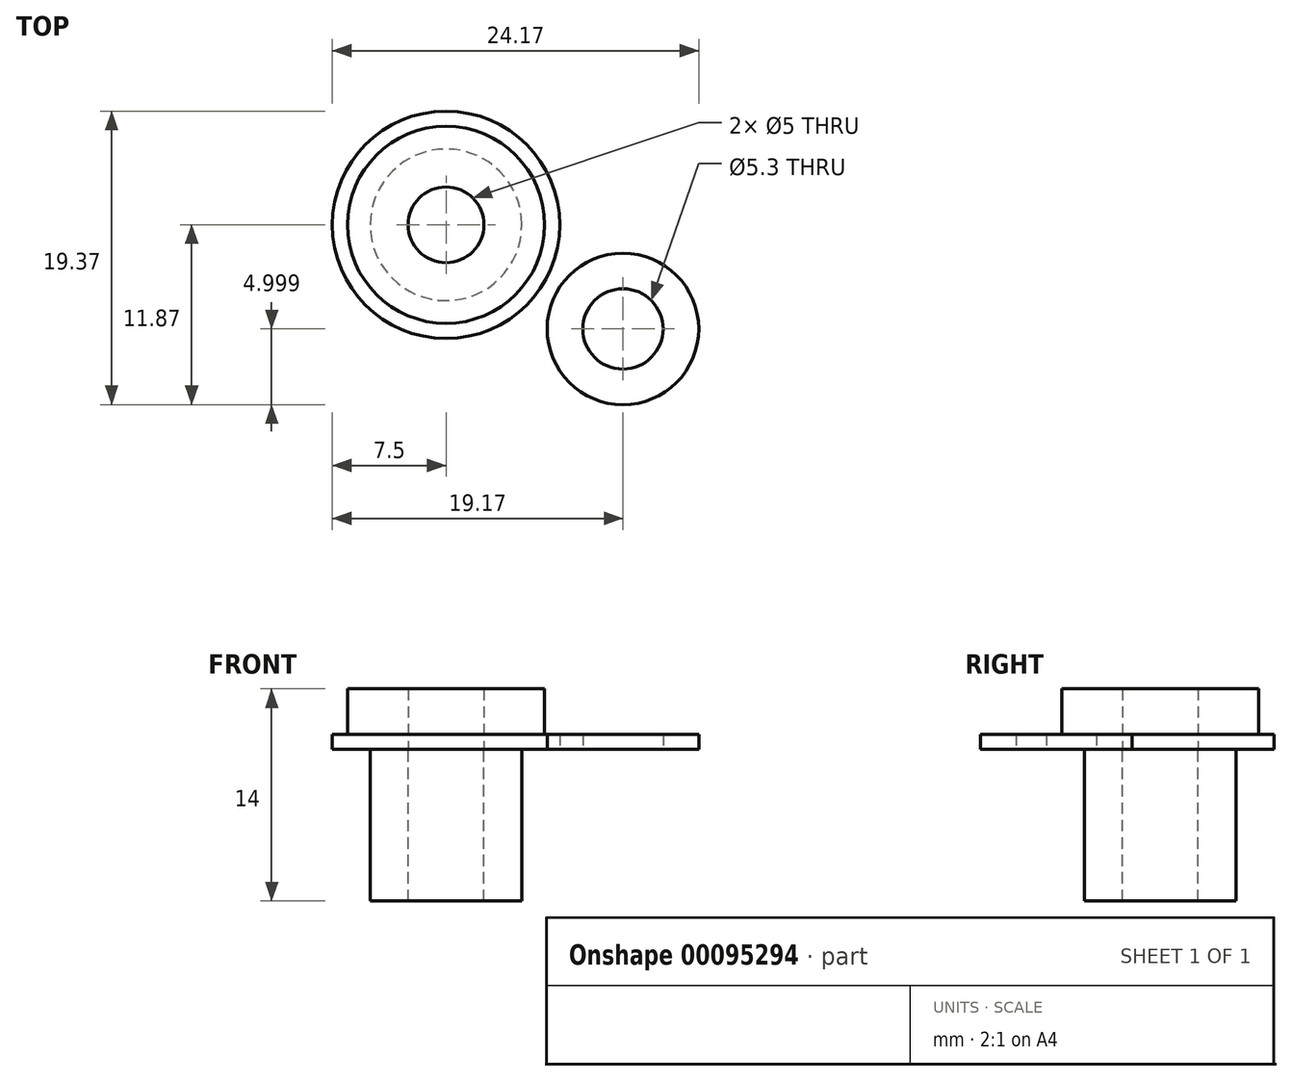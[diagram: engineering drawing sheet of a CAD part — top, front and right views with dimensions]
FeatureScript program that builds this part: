
annotation { "Feature Type Name" : "Feature", "Feature Type Description" : "" }
export const myFeature = defineFeature(function(context is Context, id is Id, definition is map)
    precondition{}
    {
        {
            var Q0;
            Q0=qCreatedBy(makeId("Top.planeOp"),FACE);
            var sketch = newSketch(context, id + "F0", { "sketchPlane" : qUnion([Q0])});
            skCircle(sketch, "E0", {"center": v(0, 0) * mm, "radius": 7.5 * mm});
            skCircle(sketch, "E1", {"center": v(0, 0) * mm, "radius": 6.5 * mm});
            skCircle(sketch, "E2", {"center": v(0, 0) * mm, "radius": 2.5 * mm});
            skSolve(sketch);
        }
        {
            var Q0;
            Q0=makeQuery(id+"F0.imprint","IMPRINT",FACE,{"disambiguationData":[TD([[makeQuery(id+"F0.imprint","IMPRINT",EDGE,{"derivedFrom":sQuery(id+"F0.wireOp",EDGE,"E0")}),1.0]])]});
            var Q1;
            Q1=makeQuery(id+"F0.imprint","IMPRINT",FACE,{"disambiguationData":[TD([[makeQuery(id+"F0.imprint","IMPRINT",EDGE,{"derivedFrom":sQuery(id+"F0.wireOp",EDGE,"E1")}),1.0]])]});
            extrude(context, id + "F1", {"entities" : qUnion([Q0, Q1]), "depth" : 1 * mm});
        }
        {
            var Q0;
            Q0=makeQuery(id+"F0.imprint","IMPRINT",FACE,{"disambiguationData":[TD([[makeQuery(id+"F0.imprint","IMPRINT",EDGE,{"derivedFrom":sQuery(id+"F0.wireOp",EDGE,"E1")}),1.0]])]});
            extrude(context, id + "F2", {"entities" : qUnion([Q0]), "operationType" : NewBodyOperationType.ADD, "depth" : 4 * mm});
        }
        {
            var Q0;
            Q0=makeQuery(id+"F1.opExtrude","CAP_FACE",FACE,{"disambiguationData":[OSD([sQuery(id+"F0.wireOp",EDGE,"E0")])],"isStart":true});
            var sketch = newSketch(context, id + "F3", { "sketchPlane" : qUnion([Q0])});
            skCircle(sketch, "E3.0", {"center": v(0, 0) * mm, "radius": 2.5 * mm});
            skCircle(sketch, "E4", {"center": v(0, 0) * mm, "radius": 5 * mm});
            skSolve(sketch);
        }
        {
            var Q0;
            Q0 = qSketchRegion(id + "F3", true);
            extrude(context, id + "F4", {"entities" : qUnion([Q0]), "depth" : 10 * mm});
        }
        {
            var Q0;
            Q0=qCreatedBy(makeId("Top.planeOp"),FACE);
            var sketch = newSketch(context, id + "F5", { "sketchPlane" : qUnion([Q0])});
            skCircle(sketch, "E5", {"center": v(11.67, -6.87) * mm, "radius": 5 * mm});
            skCircle(sketch, "E6", {"center": v(11.67, -6.87) * mm, "radius": 2.65 * mm});
            skSolve(sketch);
        }
        {
            var Q0;
            Q0 = qSketchRegion(id + "F5", true);
            extrude(context, id + "F6", {"entities" : qUnion([Q0]), "depth" : 1 * mm});
        }
    });
